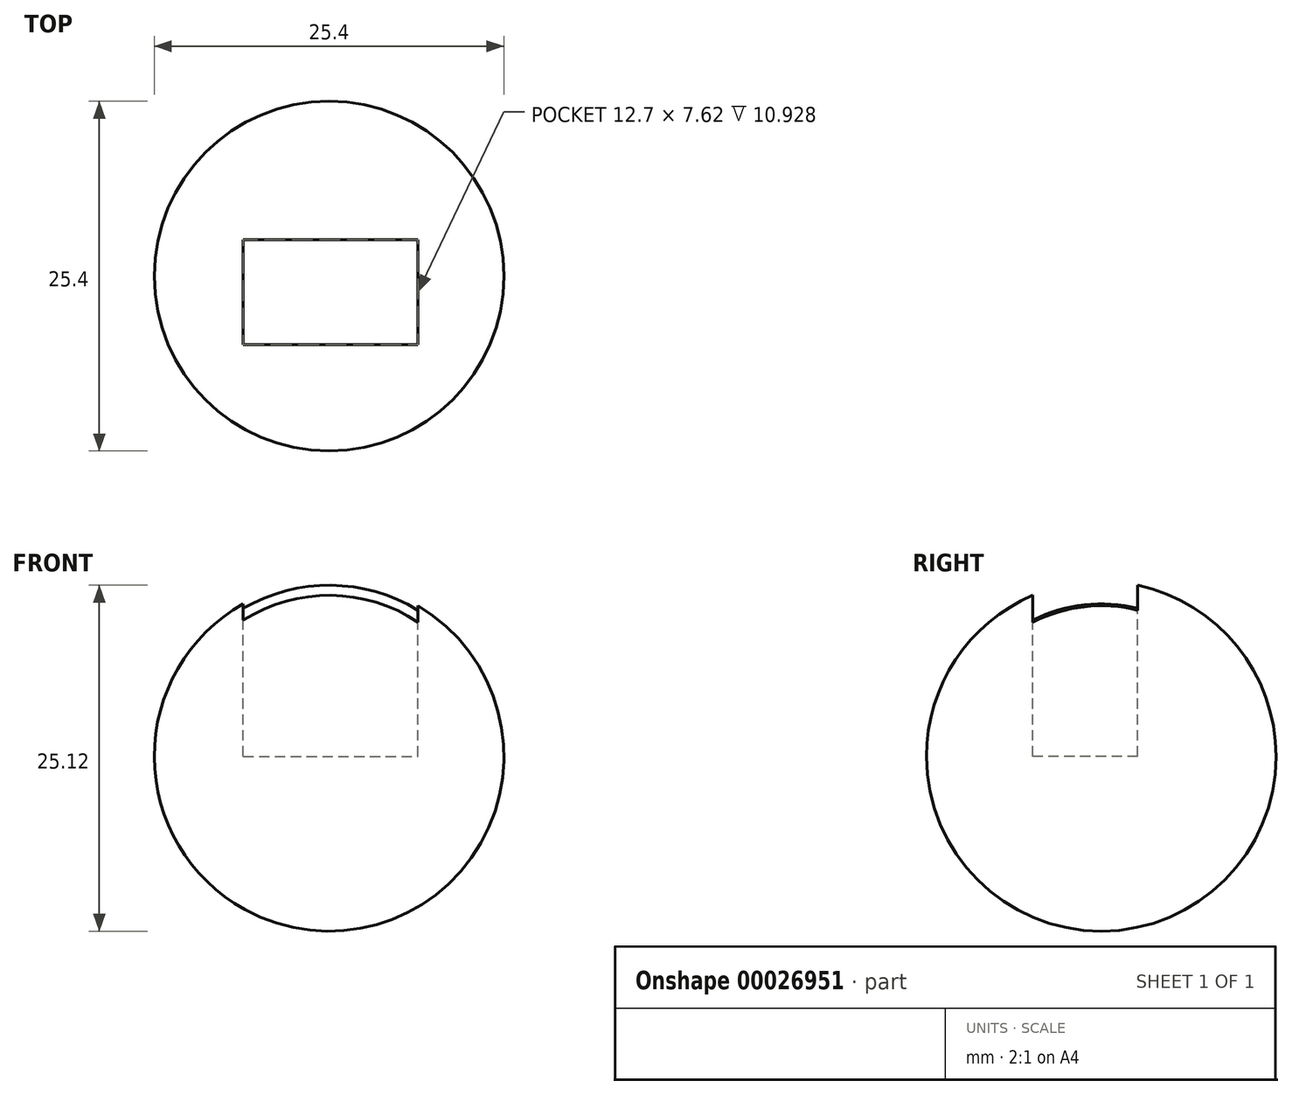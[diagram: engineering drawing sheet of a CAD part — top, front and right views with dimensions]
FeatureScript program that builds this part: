
annotation { "Feature Type Name" : "Feature", "Feature Type Description" : "" }
export const myFeature = defineFeature(function(context is Context, id is Id, definition is map)
    precondition{}
    {
        {
            var Q0;
            Q0=qCreatedBy(makeId("Top.planeOp"),FACE);
            var sketch = newSketch(context, id + "F0", { "sketchPlane" : qUnion([Q0])});
            skLineSegment(sketch, "E0", {"start": v(2.3, 10.04) * mm, "end": v(2.3, -15.36) * mm});
            skArc(sketch, "E1", {"start": v(2.3, -15.36) * mm, "mid": v(15, -2.66) * mm, "end": v(2.3, 10.04) * mm});
            skSolve(sketch);
        }
        {
            var Q0;
            Q0=makeQuery(id+"F0.imprint","IMPRINT",FACE,{"disambiguationData":[TD([[makeQuery(id+"F0.imprint","IMPRINT",EDGE,{"derivedFrom":sQuery(id+"F0.wireOp",EDGE,"E0")}),1.0]])]});
            var Q1;
            Q1=sQuery(id+"F0.wireOp",EDGE,"E0");
            revolve(context, id + "F1", {"entities" : qUnion([Q0]), "axis" : qUnion([Q1]), "revolveType" : RevolveType.FULL});
        }
        {
            var Q0;
            Q0=qCreatedBy(makeId("Top.planeOp"),FACE);
            cPlane(context, id + "F2", {"entities" : qUnion([Q0]), "cplaneType" : CPlaneType.OFFSET, "offset" : 12.7 * mm, "width" : 152.4 * mm, "height" : 152.4 * mm});
        }
        {
            var Q0;
            Q0=qCreatedBy(id+"F2.planeOp",FACE);
            var sketch = newSketch(context, id + "F3", { "sketchPlane" : qUnion([Q0])});
            skLineSegment(sketch, "E2.bottom", {"start": v(-3.93, 0) * mm, "end": v(8.77, 0) * mm});
            skLineSegment(sketch, "E2.top", {"start": v(-3.93, -7.62) * mm, "end": v(8.77, -7.62) * mm});
            skLineSegment(sketch, "E2.left", {"start": v(-3.93, 0) * mm, "end": v(-3.93, -7.62) * mm});
            skLineSegment(sketch, "E2.right", {"start": v(8.77, 0) * mm, "end": v(8.77, -7.62) * mm});
            skSolve(sketch);
        }
        {
            var Q0;
            Q0=makeQuery(id+"F3.imprint","IMPRINT",FACE,{"disambiguationData":[TD([[makeQuery(id+"F3.imprint","IMPRINT",EDGE,{"derivedFrom":sQuery(id+"F3.wireOp",EDGE,"E2.bottom")}),-1.0]])]});
            extrude(context, id + "F4", {"entities" : qUnion([Q0]), "operationType" : NewBodyOperationType.REMOVE, "oppositeDirection" : true, "depth" : 12.7 * mm});
        }
    });
